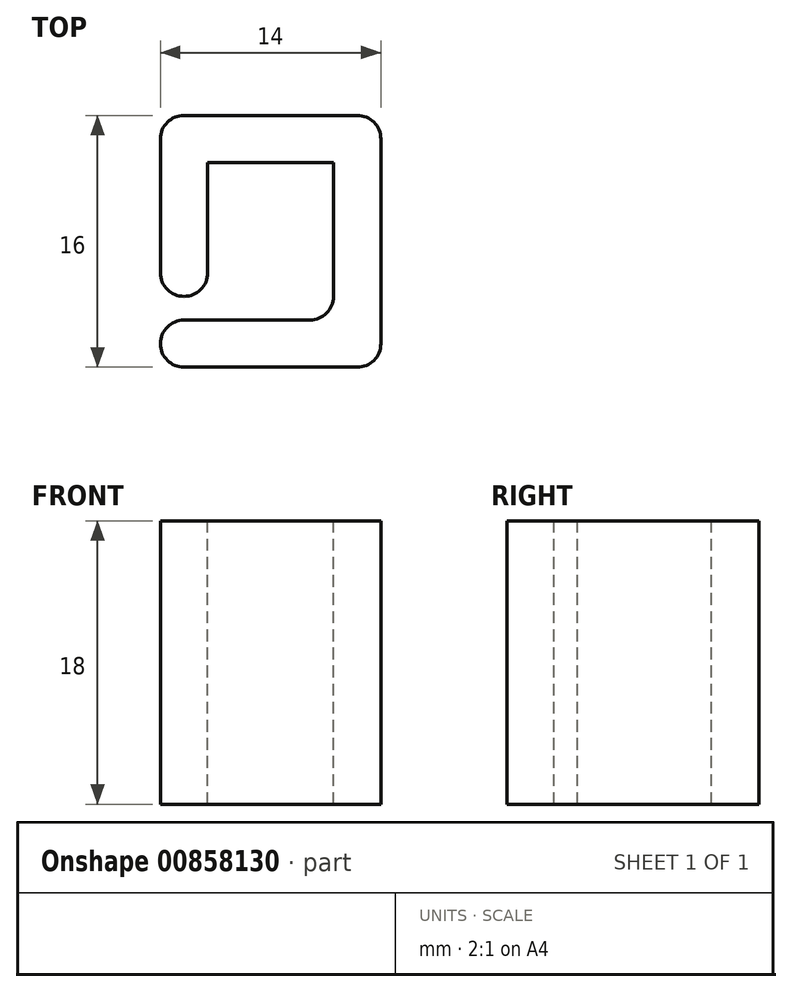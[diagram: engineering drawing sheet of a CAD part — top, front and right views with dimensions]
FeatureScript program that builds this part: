
annotation { "Feature Type Name" : "Feature", "Feature Type Description" : "" }
export const myFeature = defineFeature(function(context is Context, id is Id, definition is map)
    precondition{}
    {
        {
            var Q0;
            Q0=qCreatedBy(makeId("Front.planeOp"),FACE);
            var sketch = newSketch(context, id + "F0", { "sketchPlane" : qUnion([Q0])});
            skLineSegment(sketch, "E0.bottom", {"start": v(0, 0) * mm, "end": v(14, 0) * mm});
            skLineSegment(sketch, "E0.top", {"start": v(0, 18) * mm, "end": v(14, 18) * mm});
            skLineSegment(sketch, "E0.left", {"start": v(0, 0) * mm, "end": v(0, 18) * mm});
            skLineSegment(sketch, "E0.right", {"start": v(14, 0) * mm, "end": v(14, 18) * mm});
            skSolve(sketch);
        }
        {
            var Q0;
            Q0=makeQuery(id+"F0.imprint","IMPRINT",FACE,{"disambiguationData":[TD([[makeQuery(id+"F0.imprint","IMPRINT",EDGE,{"derivedFrom":sQuery(id+"F0.wireOp",EDGE,"E0.bottom")}),1.0]])]});
            extrude(context, id + "F1", {"entities" : qUnion([Q0]), "depth" : 3 * mm, "offsetDistance" : 25 * mm});
        }
        {
            var Q0;
            Q0=makeQuery(id+"F1.opExtrude","SWEPT_FACE",FACE,{"disambiguationData":[OSD([sQuery(id+"F0.wireOp",EDGE,"E0.top")])]});
            var sketch = newSketch(context, id + "F2", { "sketchPlane" : qUnion([Q0])});
            skLineSegment(sketch, "E1.bottom", {"start": v(0, -3) * mm, "end": v(3, -3) * mm});
            skLineSegment(sketch, "E1.top", {"start": v(0, -13) * mm, "end": v(14, -13) * mm});
            skLineSegment(sketch, "E1.left", {"start": v(0, -3) * mm, "end": v(0, -13) * mm});
            skLineSegment(sketch, "E1.right", {"start": v(14, -3) * mm, "end": v(14, -13) * mm});
            skLineSegment(sketch, "E2", {"start": v(3, -3) * mm, "end": v(3, -13) * mm});
            skLineSegment(sketch, "E3", {"start": v(11, -3) * mm, "end": v(11, -13) * mm});
            skLineSegment(sketch, "E4", {"start": v(3, -3) * mm, "end": v(11, -3) * mm});
            skLineSegment(sketch, "E5", {"start": v(11, -3) * mm, "end": v(14, -3) * mm});
            skLineSegment(sketch, "E6", {"start": v(14, -13) * mm, "end": v(14, -16) * mm});
            skLineSegment(sketch, "E7", {"start": v(14, -16) * mm, "end": v(0, -16) * mm});
            skLineSegment(sketch, "E8", {"start": v(0, -16) * mm, "end": v(0, -13) * mm});
            skLineSegment(sketch, "E9", {"start": v(0, -11.5) * mm, "end": v(3, -11.5) * mm});
            skSolve(sketch);
        }
        {
            var Q0;
            {var subQ0=sQuery(id+"F2.wireOp",EDGE,"E1.bottom");Q0=makeQuery(id+"F2.imprint","IMPRINT",FACE,{"disambiguationData":[TD([[makeQuery(id+"F2.imprint","IMPRINT",EDGE,{"derivedFrom":subQ0}),-1.0]])]});}
            var Q1;
            {var subQ0=sQuery(id+"F2.wireOp",EDGE,"E6");Q1=makeQuery(id+"F2.imprint","IMPRINT",FACE,{"disambiguationData":[TD([[makeQuery(id+"F2.imprint","IMPRINT",EDGE,{"derivedFrom":subQ0}),-1.0]])]});}
            var Q2;
            {var subQ0=sQuery(id+"F2.wireOp",EDGE,"E1.right");Q2=makeQuery(id+"F2.imprint","IMPRINT",FACE,{"disambiguationData":[TD([[makeQuery(id+"F2.imprint","IMPRINT",EDGE,{"derivedFrom":subQ0}),-1.0]])]});}
            var Q3;
            Q3=makeQuery(id+"F1.opExtrude","SWEPT_FACE",FACE,{"disambiguationData":[OSD([sQuery(id+"F0.wireOp",EDGE,"E0.bottom")])]});
            extrude(context, id + "F3", {"entities" : qUnion([Q0, Q1, Q2]), "operationType" : NewBodyOperationType.ADD, "endBound" : BoundingType.UP_TO_SURFACE, "oppositeDirection" : true, "depth" : 25 * mm, "endBoundEntityFace" : qUnion([Q3]), "offsetDistance" : 25 * mm});
        }
        {
            var Q0;
            Q0=makeQuery(id+"F3.opExtrude","SWEPT_EDGE",EDGE,{"disambiguationData":[OSD([sQuery(id+"F2.wireOp",EDGE,"E1.left"),sQuery(id+"F2.wireOp",EDGE,"E9")])]});
            var Q1;
            Q1=makeQuery(id+"F3.opExtrude","SWEPT_EDGE",EDGE,{"disambiguationData":[OSD([sQuery(id+"F2.wireOp",EDGE,"E1.top"),sQuery(id+"F2.wireOp",EDGE,"E1.left"),sQuery(id+"F2.wireOp",EDGE,"E8")])]});
            var Q2;
            Q2=makeQuery(id+"F3.opExtrude","SWEPT_EDGE",EDGE,{"disambiguationData":[OSD([sQuery(id+"F2.wireOp",EDGE,"E7"),sQuery(id+"F2.wireOp",EDGE,"E8")])]});
            var Q3;
            Q3=makeQuery(id+"F3.opExtrude","SWEPT_EDGE",EDGE,{"disambiguationData":[OSD([sQuery(id+"F2.wireOp",EDGE,"E2"),sQuery(id+"F2.wireOp",EDGE,"E9")])]});
            var Q4;
            Q4=makeQuery(id+"F3.opExtrude","SWEPT_EDGE",EDGE,{"disambiguationData":[OSD([sQuery(id+"F2.wireOp",EDGE,"E6"),sQuery(id+"F2.wireOp",EDGE,"E7")])]});
            var Q5;
            Q5=makeQuery(id+"F1.opExtrude","CAP_EDGE",EDGE,{"disambiguationData":[OSD([sQuery(id+"F0.wireOp",EDGE,"E0.right")])],"isStart":true});
            var Q6;
            Q6=makeQuery(id+"F1.opExtrude","CAP_EDGE",EDGE,{"disambiguationData":[OSD([sQuery(id+"F0.wireOp",EDGE,"E0.left")])],"isStart":true});
            var Q7;
            Q7=makeQuery(id+"F3.opExtrude","SWEPT_EDGE",EDGE,{"disambiguationData":[OSD([sQuery(id+"F2.wireOp",EDGE,"E1.bottom"),sQuery(id+"F2.wireOp",EDGE,"E2"),sQuery(id+"F2.wireOp",EDGE,"E4")])]});
            var Q8;
            Q8=makeQuery(id+"F3.opExtrude","SWEPT_EDGE",EDGE,{"disambiguationData":[OSD([sQuery(id+"F2.wireOp",EDGE,"E3"),sQuery(id+"F2.wireOp",EDGE,"E4"),sQuery(id+"F2.wireOp",EDGE,"E5")])]});
            var Q9;
            Q9=makeQuery(id+"F3.opExtrude","SWEPT_EDGE",EDGE,{"disambiguationData":[OSD([sQuery(id+"F2.wireOp",EDGE,"E1.top"),sQuery(id+"F2.wireOp",EDGE,"E3")])]});
            fillet(context, id + "F4", {"entities" : qUnion([Q0, Q1, Q2, Q3, Q4, Q5, Q6, Q7, Q8, Q9]), "radius" : 1.5 * mm, "tangentPropagation" : true, "allowEdgeOverflow" : false});
        }
    });
